FCSTD DOCUMENT  (FreeCAD 1.0R39319 (Git))
Label: demo3
License: All rights reserved
LicenseURL: https://en.wikipedia.org/wiki/All_rights_reserved
objects: Sketcher::SketchObject×1, PartDesign::Body×1
note: 3 computed .brp shape members not serialized (recipe doc carries the construction recipe); baked Part::Feature solids carry a one-line shape summary decoded from their .brp

FEATURE [Sketcher::SketchObject] Sketch
  ArcFitTolerance = 1e-06
  AttachmentSupport = -> [XY_Plane]
  FullyConstrained = false
  MakeInternals = false
  MapMode = 5
  sketch-geometry (13):
    g0: Circle CenterX=-34.5495 CenterY=3.8e-15 CenterZ=0 NormalX=0 NormalY=0 NormalZ=1 AngleXU=0 Radius=12.5
    g1: ArcOfCircle CenterX=-35.0962 CenterY=0 CenterZ=0 NormalX=0 NormalY=0 NormalZ=1 AngleXU=0 Radius=30 StartAngle=1.87201 EndAngle=5.5656
    g2: LineSegment [constr] StartX=-34.5495 StartY=3.8e-15 StartZ=0 EndX=65.4505 EndY=5.88379 EndZ=0
    g3: LineSegment [constr] StartX=65.4505 StartY=5.88379 StartZ=0 EndX=10.355 EndY=89.5444 EndZ=0
    g4: LineSegment [constr] StartX=10.355 StartY=89.5444 StartZ=0 EndX=-34.5495 EndY=3.8e-15 EndZ=0
    g5: Circle [constr] CenterX=13.752 CenterY=31.8094 CenterZ=0 NormalX=0 NormalY=0 NormalZ=1 AngleXU=0 Radius=57.8349
    g6: Circle CenterX=67.1017 CenterY=0 CenterZ=0 NormalX=0 NormalY=0 NormalZ=1 AngleXU=0 Radius=12.5
    g7: ArcOfCircle CenterX=67.1017 CenterY=0 CenterZ=0 NormalX=0 NormalY=0 NormalZ=1 AngleXU=0 Radius=30.3134 StartAngle=3.78463 EndAngle=7.70644
    g8: Circle CenterX=10.355 CenterY=89.5444 CenterZ=0 NormalX=0 NormalY=0 NormalZ=1 AngleXU=0 Radius=9
    g9: ArcOfCircle CenterX=10.355 CenterY=89.5444 CenterZ=0 NormalX=0 NormalY=0 NormalZ=1 AngleXU=0 Radius=30 StartAngle=5.99351 EndAngle=9.75497
    g10: ArcOfCircle CenterX=-55.8635 CenterY=66.8485 CenterZ=0 NormalX=0 NormalY=0 NormalZ=1 AngleXU=0 Radius=40 StartAngle=5.0136 EndAngle=6.61338
    g11: ArcOfCircle CenterX=15.952 CenterY=-46.4362 CenterZ=0 NormalX=0 NormalY=0 NormalZ=1 AngleXU=0 Radius=39.009 StartAngle=0.810215 EndAngle=2.40347
    g12: ArcOfCircle CenterX=77.4386 CenterY=69.5494 CenterZ=0 NormalX=0 NormalY=0 NormalZ=1 AngleXU=0 Radius=40 StartAngle=2.85192 EndAngle=4.56484
  constraints (33):
    c: Diameter(g0) = 25
    c: PointOnObject(g0,g-1)
    c: Diameter(g1) = 60
    c: PointOnObject(g1,g-1)
    c: Coincident(g2,g3)
    c: Coincident(g3,g4)
    c: Coincident(g4,g2)
    c: Equal(g2,g3)
    c: Equal(g2,g4)
    c: PointOnObject(g2,g5)
    c: PointOnObject(g3,g5)
    c: PointOnObject(g4,g5)
    c: Coincident(g4,g0)
    c: DistanceX(g2,g2) = 100
    c: Diameter(g6) = 25
    c: PointOnObject(g6,g-1)
    c: Coincident(g7,g6)
    c: Diameter(g8) = 18
    c: Coincident(g8,g3)
    c: Diameter(g9) = 60
    c: Coincident(g9,g3)
    c: Radius(g10) = 40
    c: Tangent(g11,g1) = 1.5708
    c: PointOnObject(g1,g5)
    c: PointOnObject(g1,g5)
    c: PointOnObject(g7,g5)
    c: Tangent(g9,g10) = 1.5708
    c: Radius(g12) = 40
    c: Tangent(g9,g12) = 1.5708
    c: PointOnObject(g7,g5)
    c: Tangent(g12,g7) = 1.5708
    c: Tangent(g10,g1) = 1.5708
    c: Coincident(g11,g7)
FEATURE [PartDesign::Body] Body
  AllowCompound = false
  Group = -> [Sketch]
  Origin = -> Origin
